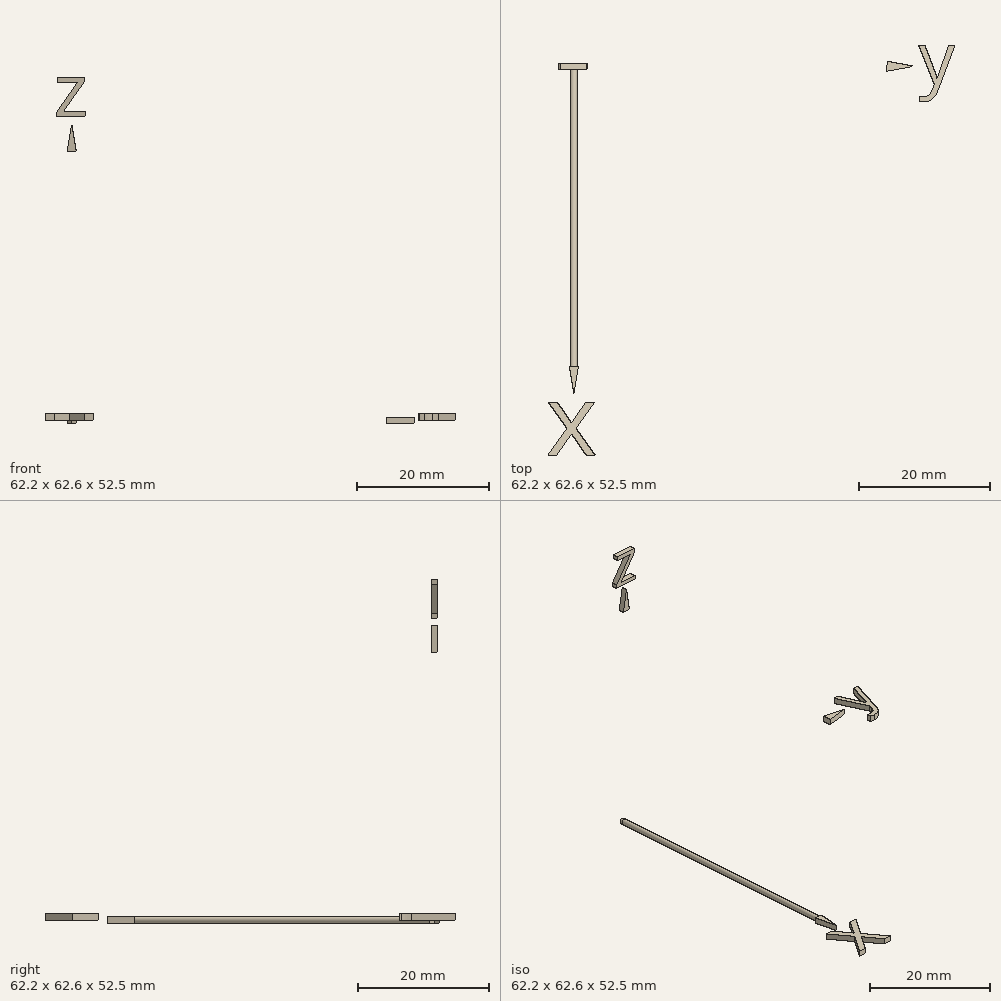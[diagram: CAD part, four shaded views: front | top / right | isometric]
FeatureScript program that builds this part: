
annotation { "Feature Type Name" : "Feature", "Feature Type Description" : "" }
export const myFeature = defineFeature(function(context is Context, id is Id, definition is map)
    precondition{}
    {
        {
            var Q0;
            Q0=qCreatedBy(makeId("Top.planeOp"),FACE);
            var sketch = newSketch(context, id + "F0", { "sketchPlane" : qUnion([Q0])});
            skCircle(sketch, "E0", {"center": v(0, 0) * mm, "radius": 37.5 * mm});
            skText(sketch, "E1", { "text": "x", "fontName": "OpenSans-Regular.ttf"});
            skLineSegment(sketch, "E2", {"start": v(0, 0) * mm, "end": v(0, -50) * mm});
            skLineSegment(sketch, "E3", {"start": v(0, -50) * mm, "end": v(0, 41.64) * mm});
            skLineSegment(sketch, "E4", {"start": v(0, 0) * mm, "end": v(52, 0) * mm});
            skLineSegment(sketch, "E5", {"start": v(52, 0) * mm, "end": v(47.84, 0.8) * mm});
            skLineSegment(sketch, "E6", {"start": v(52, 0) * mm, "end": v(47.83, -0.76) * mm});
            skText(sketch, "E7", { "text": "y\n", "fontName": "OpenSans-Regular.ttf"});
            skCircle(sketch, "E8", {"center": v(0, 0) * mm, "radius": 37.25 * mm});
            skLineSegment(sketch, "E9", {"start": v(0, 0) * mm, "end": v(41, -22.7) * mm});
            skLineSegment(sketch, "E10", {"start": v(41, -22.7) * mm, "end": v(37.49, -19.87) * mm});
            skLineSegment(sketch, "E11", {"start": v(41, -22.7) * mm, "end": v(36.76, -21.07) * mm});
            skArc(sketch, "E12", {"start": v(17.44, -9.65) * mm, "mid": v(10.12, -17.17) * mm, "end": v(0, -19.93) * mm});
            skCircle(sketch, "E13", {"center": v(0, 0) * mm, "radius": 0.5 * mm});
            skLineSegment(sketch, "E14", {"start": v(47.84, 0.8) * mm, "end": v(47.83, -0.76) * mm});
            skLineSegment(sketch, "E15", {"start": v(0, -50) * mm, "end": v(0.7, -45.83) * mm});
            skLineSegment(sketch, "E16", {"start": v(0, -50) * mm, "end": v(-0.7, -45.83) * mm});
            skLineSegment(sketch, "E17", {"start": v(-0.7, -45.83) * mm, "end": v(0.7, -45.83) * mm});
            const initialGuessF0  = {"E1": [-0.00427, -0.05945, 1, 0, 0.0108], "E7": [0.05266, -0.00276, 1, 0, 0.008]};
            skSetInitialGuess(sketch, initialGuessF0);
            skSolve(sketch);
        }
        {
            var Q0;
            Q0=qCreatedBy(makeId("Front.planeOp"),FACE);
            var sketch = newSketch(context, id + "F1", { "sketchPlane" : qUnion([Q0])});
            skLineSegment(sketch, "E18", {"start": v(0, 0) * mm, "end": v(0, 45) * mm});
            skLineSegment(sketch, "E19", {"start": v(0, 45) * mm, "end": v(-0.7, 40.83) * mm});
            skLineSegment(sketch, "E20", {"start": v(0, 45) * mm, "end": v(0.7, 40.83) * mm});
            skText(sketch, "E21", { "text": "z", "fontName": "OpenSans-Regular.ttf"});
            skCircle(sketch, "E22", {"center": v(0, 0) * mm, "radius": 0.5 * mm});
            skLineSegment(sketch, "E23", {"start": v(-0.7, 40.83) * mm, "end": v(0.7, 40.83) * mm});
            const initialGuessF1  = {"E21": [-0.00274, 0.0461, 1, 0, 0.008]};
            skSetInitialGuess(sketch, initialGuessF1);
            skSolve(sketch);
        }
        {
            var Q0;
            Q0=sQuery(id+"F0.wireOp",VERTEX,"E9.end");
            var Q1;
            Q1=sQuery(id+"F0.wireOp",VERTEX,"E2.start");
            var Q2;
            Q2=sQuery(id+"F1.wireOp",VERTEX,"E20.start");
            cPlane(context, id + "F2", {"entities" : qUnion([Q0, Q1, Q2]), "cplaneType" : CPlaneType.THREE_POINT, "offset" : 25 * mm, "width" : 150 * mm, "height" : 150 * mm});
        }
        {
            var Q0;
            Q0=qSketchRegion(id+"F1",true);
            extrude(context, id + "F3", {"entities" : qUnion([Q0]), "endBound" : BoundingType.SYMMETRIC, "depth" : 1 * mm, "offsetDistance" : 25 * mm});
        }
        {
            var Q0;
            Q0=makeQuery(id+"F0.imprint","IMPRINT",FACE,{"disambiguationData":[TD([[makeQuery(id+"F0.imprint","IMPRINT",EDGE,{"derivedFrom":sQuery(id+"F0.wireOp",EDGE,"E1.sketch_text.stroke-0")}),-1.0]])]});
            extrude(context, id + "F4", {"entities" : qUnion([Q0]), "depth" : 1 * mm, "offsetDistance" : 25 * mm});
        }
        {
            var Q0;
            Q0=makeQuery(id+"F0.imprint","IMPRINT",FACE,{"disambiguationData":[TD([[makeQuery(id+"F0.imprint","IMPRINT",EDGE,{"derivedFrom":sQuery(id+"F0.wireOp",EDGE,"E7.sketch_text.stroke-0")}),-1.0]])]});
            extrude(context, id + "F5", {"entities" : qUnion([Q0]), "depth" : 1 * mm, "offsetDistance" : 25 * mm});
        }
        {
            var Q0;
            Q0=makeQuery(id+"F1.imprint","IMPRINT",FACE,{"disambiguationData":[TD([[makeQuery(id+"F1.imprint","IMPRINT",EDGE,{"derivedFrom":sQuery(id+"F1.wireOp",EDGE,"E22")}),1.0]])]});
            extrude(context, id + "F6", {"entities" : qUnion([Q0]), "depth" : 47 * mm, "offsetDistance" : 25 * mm});
        }
        {
            var Q0;
            Q0=qCreatedBy(makeId("Right.planeOp"),FACE);
            var sketch = newSketch(context, id + "F7", { "sketchPlane" : qUnion([Q0])});
            skCircle(sketch, "E24", {"center": v(0, 0) * mm, "radius": 0.5 * mm});
            skSolve(sketch);
        }
        {
            var Q0;
            Q0=sQuery(id+"F7.wireOp",EDGE,"E24");
            extrude(context, id + "F8", {"bodyType" : ToolBodyType.SURFACE, "surfaceEntities" : qUnion([Q0]), "depth" : 49 * mm, "offsetDistance" : 25 * mm});
        }
        {
            var Q0;
            Q0=sQuery(id+"F0.wireOp",EDGE,"E13");
            extrude(context, id + "F9", {"bodyType" : ToolBodyType.SURFACE, "surfaceEntities" : qUnion([Q0]), "depth" : 41.5 * mm, "offsetDistance" : 25 * mm});
        }
        {
            var Q0;
            {var subQ0=sQuery(id+"F0.wireOp",EDGE,"E16");Q0=makeQuery(id+"F0.imprint","IMPRINT",FACE,{"disambiguationData":[TD([[makeQuery(id+"F0.imprint","IMPRINT",EDGE,{"derivedFrom":subQ0}),-1.0]])]});}
            var Q1;
            {var subQ0=sQuery(id+"F0.wireOp",EDGE,"E15");Q1=makeQuery(id+"F0.imprint","IMPRINT",FACE,{"disambiguationData":[TD([[makeQuery(id+"F0.imprint","IMPRINT",EDGE,{"derivedFrom":subQ0}),1.0]])]});}
            extrude(context, id + "F10", {"entities" : qUnion([Q0, Q1]), "operationType" : NewBodyOperationType.ADD, "endBound" : BoundingType.SYMMETRIC, "depth" : 1 * mm, "offsetDistance" : 25 * mm});
        }
        {
            var Q0;
            {var subQ0=sQuery(id+"F0.wireOp",EDGE,"E5");Q0=makeQuery(id+"F0.imprint","IMPRINT",FACE,{"disambiguationData":[TD([[makeQuery(id+"F0.imprint","IMPRINT",EDGE,{"derivedFrom":subQ0}),1.0]])]});}
            var Q1;
            {var subQ0=sQuery(id+"F0.wireOp",EDGE,"E6");Q1=makeQuery(id+"F0.imprint","IMPRINT",FACE,{"disambiguationData":[TD([[makeQuery(id+"F0.imprint","IMPRINT",EDGE,{"derivedFrom":subQ0}),-1.0]])]});}
            extrude(context, id + "F11", {"entities" : qUnion([Q0, Q1]), "endBound" : BoundingType.SYMMETRIC, "depth" : 1 * mm, "offsetDistance" : 25 * mm});
        }
    });
